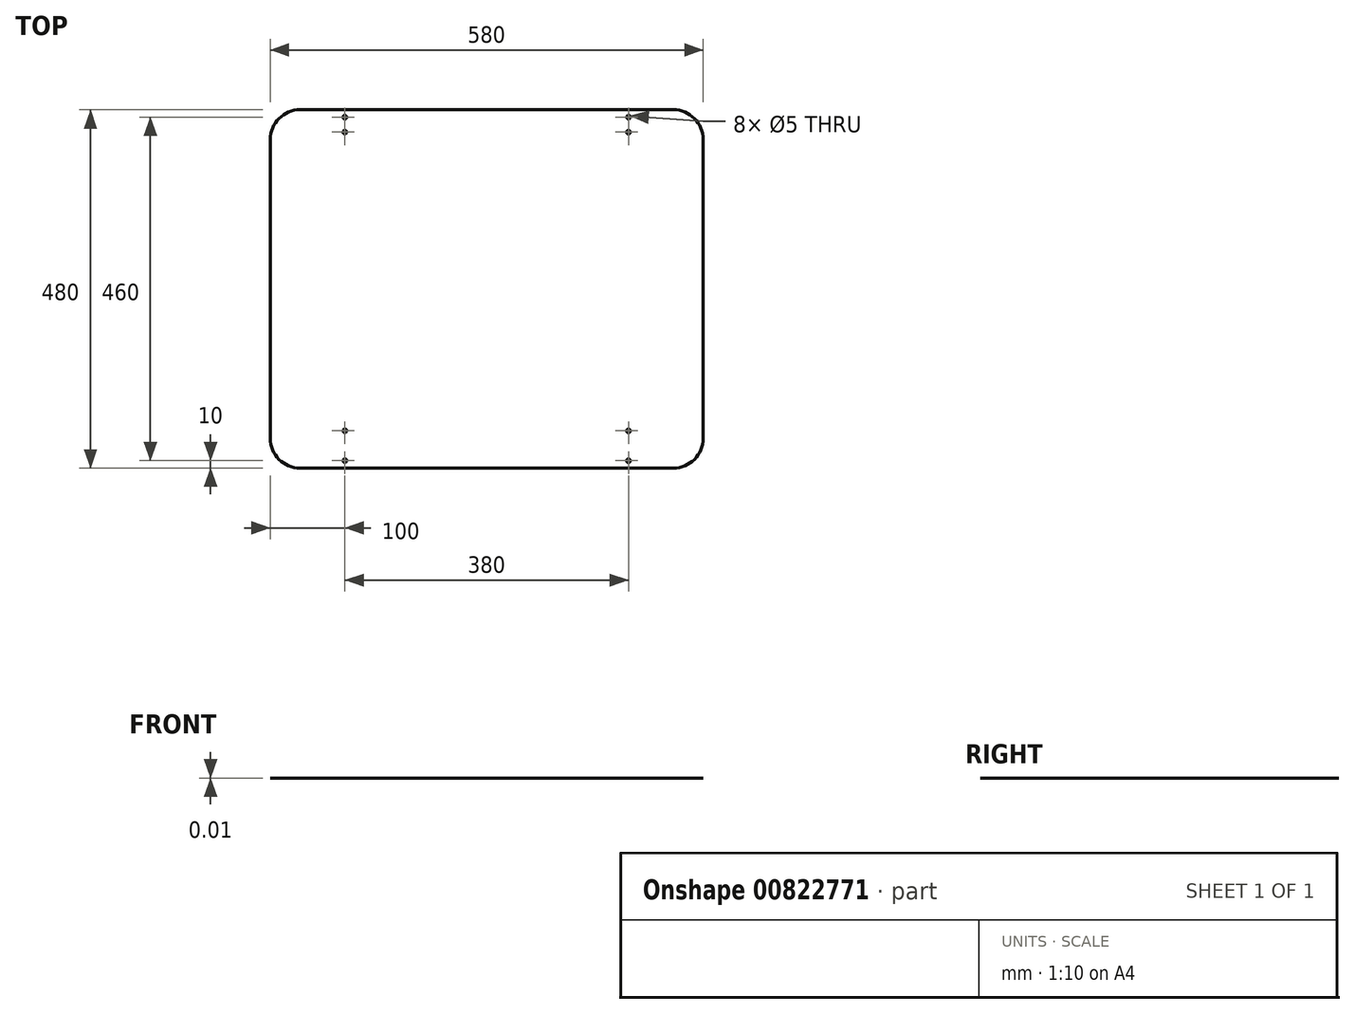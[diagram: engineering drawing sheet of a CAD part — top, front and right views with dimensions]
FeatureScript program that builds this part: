
annotation { "Feature Type Name" : "Feature", "Feature Type Description" : "" }
export const myFeature = defineFeature(function(context is Context, id is Id, definition is map)
    precondition{}
    {
        {
            var Q0;
            Q0=qCreatedBy(makeId("Top.planeOp"),FACE);
            var sketch = newSketch(context, id + "F0", { "sketchPlane" : qUnion([Q0])});
            skCircle(sketch, "E0.9", {"center": v(190, 210) * mm, "radius": 2.5 * mm});
            skCircle(sketch, "E0.10", {"center": v(190, 230) * mm, "radius": 2.5 * mm});
            skPoint(sketch, "E1.0", {"position": v(0, 0) * mm});
            skLineSegment(sketch, "E2", {"start": v(-25, 0) * mm, "end": v(25, 0) * mm, "construction": true});
            skLineSegment(sketch, "E3.bottom", {"start": v(250, -240) * mm, "end": v(-250, -240) * mm});
            skLineSegment(sketch, "E3.top", {"start": v(250, 240) * mm, "end": v(-250, 240) * mm});
            skLineSegment(sketch, "E3.left", {"start": v(290, -200) * mm, "end": v(290, 200) * mm});
            skLineSegment(sketch, "E3.right", {"start": v(-290, -200) * mm, "end": v(-290, 200) * mm});
            skPoint(sketch, "E4.visualSharp", {"position": v(-290, 240) * mm});
            skArc(sketch, "E4.filletArc", {"start": v(-250, 240) * mm, "mid": v(-278.28, 228.28) * mm, "end": v(-290, 200) * mm});
            skPoint(sketch, "E5.visualSharp", {"position": v(290, 240) * mm});
            skArc(sketch, "E5.filletArc", {"start": v(290, 200) * mm, "mid": v(278.28, 228.28) * mm, "end": v(250, 240) * mm});
            skPoint(sketch, "E6.visualSharp", {"position": v(290, -240) * mm});
            skArc(sketch, "E6.filletArc", {"start": v(250, -240) * mm, "mid": v(278.28, -228.28) * mm, "end": v(290, -200) * mm});
            skPoint(sketch, "E7.visualSharp", {"position": v(-290, -240) * mm});
            skArc(sketch, "E7.filletArc", {"start": v(-290, -200) * mm, "mid": v(-278.28, -228.28) * mm, "end": v(-250, -240) * mm});
            skCircle(sketch, "E8.MirrorC", {"center": v(190, -230) * mm, "radius": 2.5 * mm});
            skCircle(sketch, "E9.MirrorC", {"center": v(190, -190) * mm, "radius": 2.5 * mm});
            skLineSegment(sketch, "E10", {"start": v(0, 25) * mm, "end": v(0, -25) * mm, "construction": true});
            skCircle(sketch, "E11.MirrorC", {"center": v(-190, -230) * mm, "radius": 2.5 * mm});
            skCircle(sketch, "E12.MirrorC", {"center": v(-190, -190) * mm, "radius": 2.5 * mm});
            skLineSegment(sketch, "E13", {"start": v(190, 230) * mm, "end": v(190, 210) * mm});
            skCircle(sketch, "E14.MirrorC", {"center": v(-190, 230) * mm, "radius": 2.5 * mm});
            skCircle(sketch, "E15.MirrorC", {"center": v(-190, 210) * mm, "radius": 2.5 * mm});
            skLineSegment(sketch, "E16", {"start": v(190, -190) * mm, "end": v(190, -230) * mm, "construction": true});
            skSolve(sketch);
        }
        {
            var Q0;
            Q0=qSketchRegion(id+"F0",true);
            extrude(context, id + "F1", {"entities" : qUnion([Q0]), "oppositeDirection" : true, "depth" : 1 / 101.6 * mm, "offsetDistance" : 25 * mm});
        }
    });
